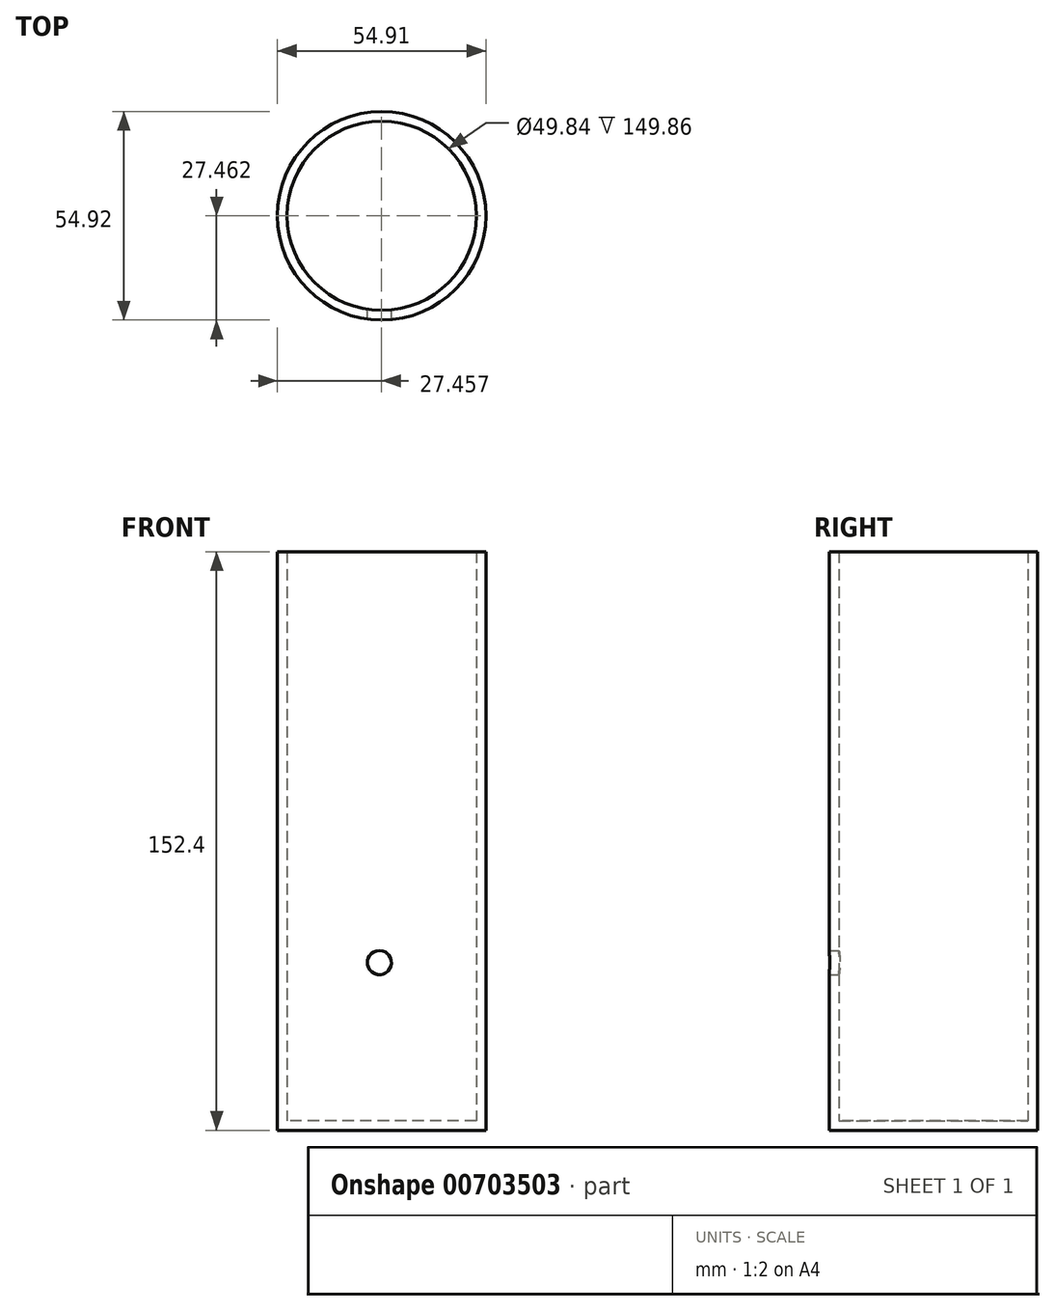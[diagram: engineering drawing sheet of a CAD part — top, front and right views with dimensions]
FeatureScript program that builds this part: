
annotation { "Feature Type Name" : "Feature", "Feature Type Description" : "" }
export const myFeature = defineFeature(function(context is Context, id is Id, definition is map)
    precondition{}
    {
        {
            var Q0;
            Q0=qCreatedBy(makeId("Top.planeOp"),FACE);
            var sketch = newSketch(context, id + "F0", { "sketchPlane" : qUnion([Q0])});
            skCircle(sketch, "E0", {"center": v(-34.61, 22.66) * mm, "radius": 27.46 * mm});
            skSolve(sketch);
        }
        {
            var Q0;
            Q0=makeQuery(id+"F0.imprint","IMPRINT",FACE,{"disambiguationData":[TD([[makeQuery(id+"F0.imprint","IMPRINT",EDGE,{"derivedFrom":sQuery(id+"F0.wireOp",EDGE,"E0")}),1.0]])]});
            extrude(context, id + "F1", {"entities" : qUnion([Q0]), "depth" : 152.4 * mm, "offsetDistance" : 25.4 * mm});
        }
        {
            var Q0;
            Q0=makeQuery(id+"F1.opExtrude","CAP_FACE",FACE,{"disambiguationData":[OSD([sQuery(id+"F0.wireOp",EDGE,"E0")])],"isStart":false});
            shell(context, id + "F2", {"entities" : qUnion([Q0]), "thickness" : 2.54 * mm});
        }
        {
            var Q0;
            Q0=qCreatedBy(makeId("Front.planeOp"),FACE);
            var sketch = newSketch(context, id + "F3", { "sketchPlane" : qUnion([Q0])});
            skPoint(sketch, "E1", {"position": v(-35.2, 44.17) * mm});
            skSolve(sketch);
        }
        {
            var Q0;
            Q0=sQuery(id+"F3.wireOp",VERTEX,"E1");
            var Q1;
            Q1=makeQuery(id+"F1.opExtrude","SWEPT_BODY",BODY,{"disambiguationData":[OSD([sQuery(id+"F0.wireOp",EDGE,"E0")])]});
            hole(context, id + "F4", {"style" : HoleStyle.SIMPLE, "endStyle" : HoleEndStyle.BLIND, "oppositeDirection" : true, "holeDiameter" : 6.35 * mm, "majorDiameter" : 6.35 * mm, "holeDepth" : 12.7 * mm, "isTappedThrough" : true, "tappedDepth" : 12.7 * mm, "tapClearance" : 3, "locations" : qUnion([Q0]), "scope" : qUnion([Q1])});
        }
    });
